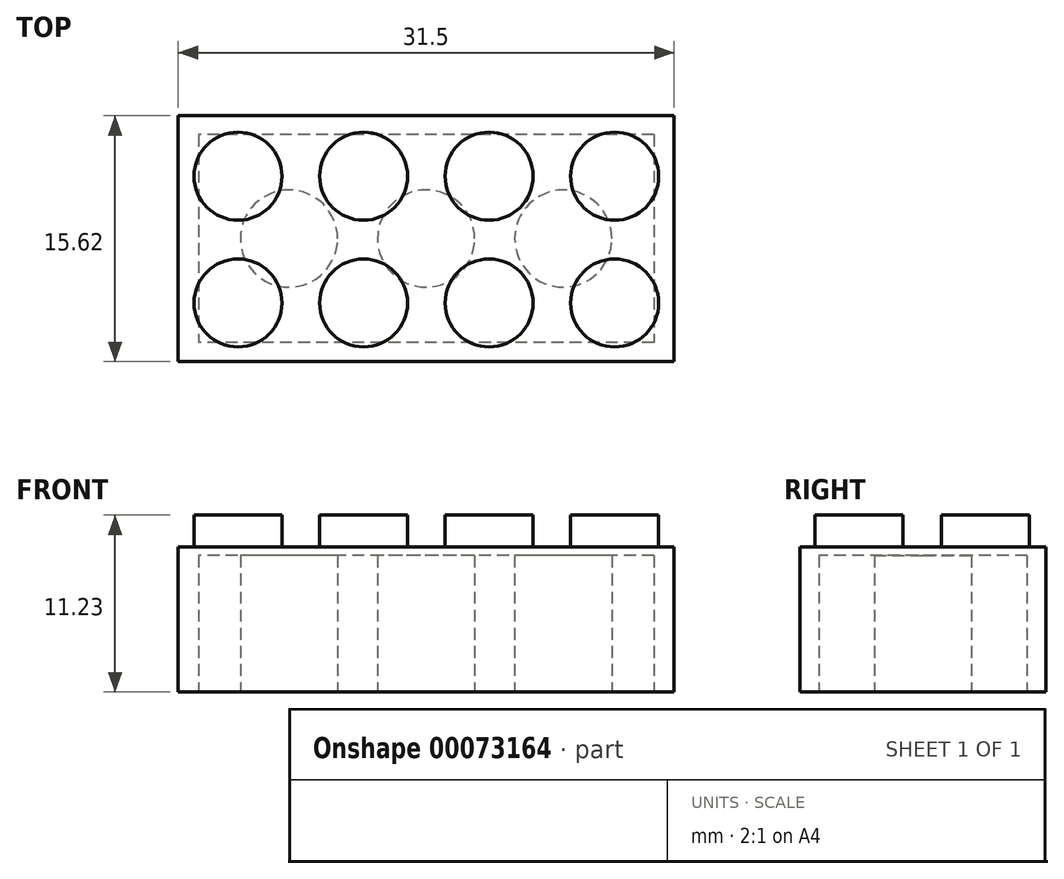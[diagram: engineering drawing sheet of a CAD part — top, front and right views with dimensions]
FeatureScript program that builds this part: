
annotation { "Feature Type Name" : "Feature", "Feature Type Description" : "" }
export const myFeature = defineFeature(function(context is Context, id is Id, definition is map)
    precondition{}
    {
        {
            var Q0;
            Q0=qCreatedBy(makeId("Top.planeOp"),FACE);
            var sketch = newSketch(context, id + "F0", { "sketchPlane" : qUnion([Q0])});
            skLineSegment(sketch, "E0.bottom", {"start": v(15.75, -7.81) * mm, "end": v(-15.75, -7.81) * mm});
            skLineSegment(sketch, "E0.top", {"start": v(15.75, 7.81) * mm, "end": v(-15.75, 7.81) * mm});
            skLineSegment(sketch, "E0.left", {"start": v(15.75, -7.81) * mm, "end": v(15.75, 7.81) * mm});
            skLineSegment(sketch, "E0.right", {"start": v(-15.75, -7.81) * mm, "end": v(-15.75, 7.81) * mm});
            skPoint(sketch, "E0.middle", {"position": v(0, 0) * mm});
            skSolve(sketch);
        }
        {
            var Q0;
            Q0=makeQuery(id+"F0.imprint","IMPRINT",FACE,{"disambiguationData":[TD([[makeQuery(id+"F0.imprint","IMPRINT",EDGE,{"derivedFrom":sQuery(id+"F0.wireOp",EDGE,"E0.bottom")}),-1.0]])]});
            extrude(context, id + "F1", {"entities" : qUnion([Q0]), "depth" : 9.2 * mm});
        }
        {
            var Q0;
            Q0=makeQuery(id+"F1.opExtrude","CAP_FACE",FACE,{"disambiguationData":[OSD([sQuery(id+"F0.wireOp",EDGE,"E0.bottom"),sQuery(id+"F0.wireOp",EDGE,"E0.top"),sQuery(id+"F0.wireOp",EDGE,"E0.left"),sQuery(id+"F0.wireOp",EDGE,"E0.right")])],"isStart":false});
            cPlane(context, id + "F2", {"entities" : qUnion([Q0]), "cplaneType" : CPlaneType.OFFSET, "offset" : 0 * mm, "width" : 152.4 * mm, "height" : 152.4 * mm});
        }
        {
            var Q0;
            Q0=qCreatedBy(id+"F2.planeOp",FACE);
            var sketch = newSketch(context, id + "F3", { "sketchPlane" : qUnion([Q0])});
            skCircle(sketch, "E1", {"center": v(-11.95, 3.96) * mm, "radius": 2.8 * mm});
            skLineSegment(sketch, "E2.0", {"start": v(-15.75, -7.81) * mm, "end": v(-15.75, 7.81) * mm});
            skLineSegment(sketch, "E3", {"start": v(-11.95, 3.96) * mm, "end": v(-15.75, 3.96) * mm, "construction": true});
            skLineSegment(sketch, "E4.0", {"start": v(15.75, 7.81) * mm, "end": v(-15.75, 7.81) * mm});
            skLineSegment(sketch, "E5", {"start": v(-11.95, 3.96) * mm, "end": v(-11.95, 7.81) * mm, "construction": true});
            skLineSegment(sketch, "E6.1.0.0", {"start": v(-3.98, 3.96) * mm, "end": v(-3.98, 7.81) * mm, "construction": true});
            skCircle(sketch, "E6.1.0.1", {"center": v(-3.98, 3.96) * mm, "radius": 2.8 * mm});
            skLineSegment(sketch, "E6.2.0.0", {"start": v(4, 3.96) * mm, "end": v(4, 7.81) * mm, "construction": true});
            skCircle(sketch, "E6.2.0.1", {"center": v(4, 3.96) * mm, "radius": 2.8 * mm});
            skLineSegment(sketch, "E6.3.0.0", {"start": v(11.98, 3.96) * mm, "end": v(11.98, 7.81) * mm, "construction": true});
            skCircle(sketch, "E6.3.0.1", {"center": v(11.98, 3.96) * mm, "radius": 2.8 * mm});
            skLineSegment(sketch, "E6.direction1", {"start": v(-11.95, 3.96) * mm, "end": v(-3.98, 3.96) * mm, "construction": true});
            skCircle(sketch, "E7.0.1.0", {"center": v(-11.95, -4.08) * mm, "radius": 2.8 * mm});
            skCircle(sketch, "E7.0.1.1", {"center": v(-3.98, -4.08) * mm, "radius": 2.8 * mm});
            skCircle(sketch, "E7.0.1.2", {"center": v(4, -4.08) * mm, "radius": 2.8 * mm});
            skCircle(sketch, "E7.0.1.3", {"center": v(11.98, -4.08) * mm, "radius": 2.8 * mm});
            skLineSegment(sketch, "E7.direction1", {"start": v(-11.95, 3.96) * mm, "end": v(-47.55, 3.96) * mm, "construction": true});
            skLineSegment(sketch, "E7.direction2", {"start": v(-11.95, 3.96) * mm, "end": v(-11.95, -4.08) * mm, "construction": true});
            skSolve(sketch);
        }
        {
            var Q0;
            Q0 = qSketchRegion(id + "F3", true);
            extrude(context, id + "F4", {"entities" : qUnion([Q0]), "operationType" : NewBodyOperationType.ADD, "depth" : 2.03 * mm});
        }
        {
            var Q0;
            Q0=qCreatedBy(makeId("Top.planeOp"),FACE);
            var sketch = newSketch(context, id + "F5", { "sketchPlane" : qUnion([Q0])});
            skLineSegment(sketch, "E8.0.0", {"start": v(15.75, -7.81) * mm, "end": v(-15.75, -7.81) * mm});
            skLineSegment(sketch, "E8.0.1", {"start": v(-15.75, -7.81) * mm, "end": v(-15.75, 7.81) * mm});
            skLineSegment(sketch, "E8.0.2", {"start": v(-15.75, 7.81) * mm, "end": v(15.75, 7.81) * mm});
            skLineSegment(sketch, "E8.0.3", {"start": v(15.75, 7.81) * mm, "end": v(15.75, -7.81) * mm});
            skLineSegment(sketch, "E9.bottom", {"start": v(14.47, 6.6) * mm, "end": v(-14.47, 6.6) * mm});
            skLineSegment(sketch, "E9.top", {"start": v(14.47, -6.6) * mm, "end": v(-14.47, -6.6) * mm});
            skLineSegment(sketch, "E9.left", {"start": v(14.47, 6.6) * mm, "end": v(14.47, -6.6) * mm});
            skLineSegment(sketch, "E9.right", {"start": v(-14.47, 6.6) * mm, "end": v(-14.47, -6.6) * mm});
            skPoint(sketch, "E9.middle", {"position": v(0, 0) * mm});
            skSolve(sketch);
        }
        {
            var Q0;
            Q0=makeQuery(id+"F5.imprint","IMPRINT",FACE,{"disambiguationData":[TD([[makeQuery(id+"F5.imprint","IMPRINT",EDGE,{"derivedFrom":sQuery(id+"F5.wireOp",EDGE,"E9.bottom")}),1.0]])]});
            extrude(context, id + "F6", {"entities" : qUnion([Q0]), "operationType" : NewBodyOperationType.REMOVE, "depth" : 8.66 * mm});
        }
        {
            var Q0;
            Q0=qCreatedBy(makeId("Top.planeOp"),FACE);
            var sketch = newSketch(context, id + "F7", { "sketchPlane" : qUnion([Q0])});
            skCircle(sketch, "E10", {"center": v(0, 0) * mm, "radius": 3.09 * mm});
            skCircle(sketch, "E11.1.0.0", {"center": v(8.71, 0) * mm, "radius": 3.09 * mm});
            skLineSegment(sketch, "E11.direction1", {"start": v(0, 0) * mm, "end": v(8.71, 0) * mm, "construction": true});
            skCircle(sketch, "E12.2.0.0", {"center": v(-8.71, 0) * mm, "radius": 3.09 * mm});
            skLineSegment(sketch, "E12.direction1", {"start": v(8.71, 0) * mm, "end": v(0, 0) * mm, "construction": true});
            skSolve(sketch);
        }
        {
            var Q0;
            Q0 = qSketchRegion(id + "F7", true);
            extrude(context, id + "F8", {"entities" : qUnion([Q0]), "operationType" : NewBodyOperationType.ADD, "depth" : 8.66 * mm});
        }
    });
